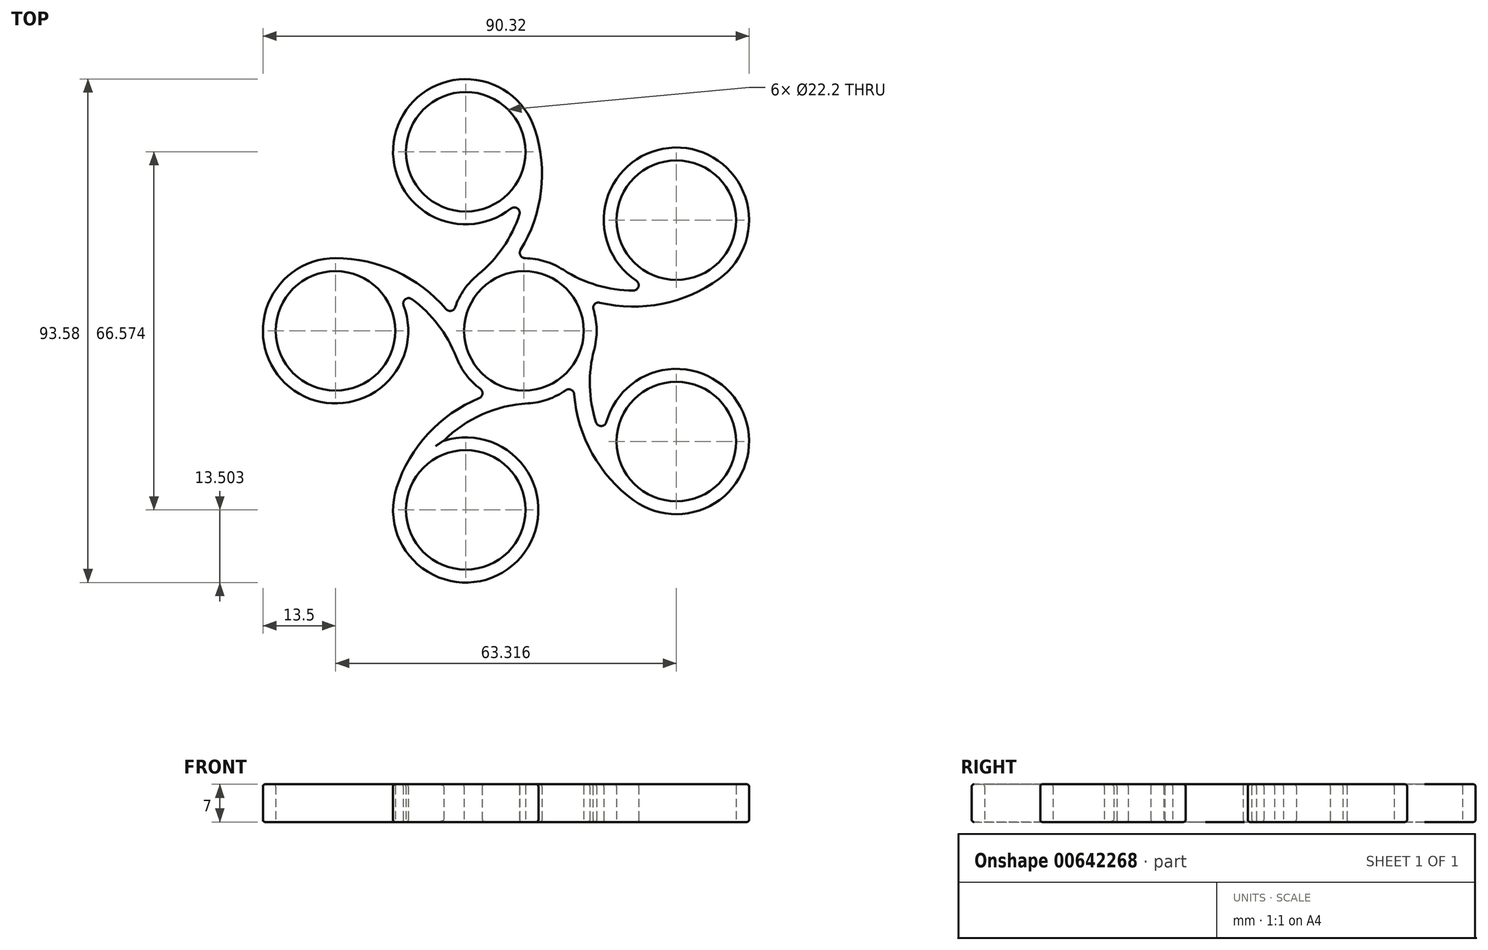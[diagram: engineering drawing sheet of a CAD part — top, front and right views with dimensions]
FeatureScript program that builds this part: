
annotation { "Feature Type Name" : "Feature", "Feature Type Description" : "" }
export const myFeature = defineFeature(function(context is Context, id is Id, definition is map)
    precondition{}
    {
        {
            var Q0;
            Q0=qCreatedBy(makeId("Top.planeOp"),FACE);
            var sketch = newSketch(context, id + "F0", { "sketchPlane" : qUnion([Q0])});
            skCircle(sketch, "E0", {"center": v(0, 0) * mm, "radius": 11.1 * mm});
            skCircle(sketch, "E1", {"center": v(0, 0) * mm, "radius": 13.5 * mm});
            skLineSegment(sketch, "E2", {"start": v(0, 0) * mm, "end": v(-35, 0) * mm, "construction": true});
            skCircle(sketch, "E3", {"center": v(-35, 0) * mm, "radius": 11.1 * mm});
            skCircle(sketch, "E4", {"center": v(-35, 0) * mm, "radius": 13.5 * mm});
            skLineSegment(sketch, "E5", {"start": v(-35, 0) * mm, "end": v(-35, -13.5) * mm, "construction": true});
            skLineSegment(sketch, "E6", {"start": v(0, 0) * mm, "end": v(0, 13.5) * mm, "construction": true});
            skLineSegment(sketch, "E7", {"start": v(-35, 0) * mm, "end": v(-25.45, -9.55) * mm, "construction": true});
            skLineSegment(sketch, "E8", {"start": v(0, 0) * mm, "end": v(-9.55, 9.55) * mm});
            skLineSegment(sketch, "E9", {"start": v(0, 0) * mm, "end": v(0, -13.5) * mm, "construction": true});
            skLineSegment(sketch, "E10", {"start": v(0, 0) * mm, "end": v(-9.55, -9.55) * mm, "construction": true});
            skArc(sketch, "E11.trimOffspring", {"start": v(-12.6, -4.86) * mm, "mid": v(-17.14, 2.55) * mm, "end": v(-24.02, 7.86) * mm});
            skArc(sketch, "E12.trimOffspring", {"start": v(-13.26, 2.52) * mm, "mid": v(-22.82, 10.6) * mm, "end": v(-35, 13.5) * mm});
            skArc(sketch, "E13.1.0", {"start": v(0.73, -13.48) * mm, "mid": v(-7.72, -15.51) * mm, "end": v(-14.9, -20.42) * mm});
            skCircle(sketch, "E13.1.1", {"center": v(-10.82, -33.29) * mm, "radius": 13.5 * mm});
            skArc(sketch, "E13.1.2", {"start": v(-6.5, -11.84) * mm, "mid": v(-17.13, -18.43) * mm, "end": v(-23.65, -29.12) * mm});
            skLineSegment(sketch, "E13.1.3", {"start": v(-10.82, -33.29) * mm, "end": v(2.02, -37.46) * mm, "construction": true});
            skCircle(sketch, "E13.1.4", {"center": v(-10.82, -33.29) * mm, "radius": 11.1 * mm});
            skLineSegment(sketch, "E13.1.5", {"start": v(-10.82, -33.29) * mm, "end": v(1.21, -27.16) * mm, "construction": true});
            skArc(sketch, "E13.2.0", {"start": v(13.05, -3.47) * mm, "mid": v(12.37, -12.14) * mm, "end": v(14.82, -20.48) * mm});
            skCircle(sketch, "E13.2.1", {"center": v(28.32, -20.57) * mm, "radius": 13.5 * mm});
            skArc(sketch, "E13.2.2", {"start": v(9.25, -9.83) * mm, "mid": v(12.23, -21.99) * mm, "end": v(20.38, -31.5) * mm});
            skLineSegment(sketch, "E13.2.3", {"start": v(28.32, -20.57) * mm, "end": v(36.25, -9.65) * mm, "construction": true});
            skCircle(sketch, "E13.2.4", {"center": v(28.32, -20.57) * mm, "radius": 11.1 * mm});
            skLineSegment(sketch, "E13.2.5", {"start": v(28.32, -20.57) * mm, "end": v(26.2, -7.24) * mm, "construction": true});
            skArc(sketch, "E13.3.0", {"start": v(7.33, 11.33) * mm, "mid": v(15.36, 8.01) * mm, "end": v(24.05, 7.76) * mm});
            skCircle(sketch, "E13.3.1", {"center": v(28.32, 20.57) * mm, "radius": 13.5 * mm});
            skArc(sketch, "E13.3.2", {"start": v(12.2, 5.76) * mm, "mid": v(24.7, 4.84) * mm, "end": v(36.25, 9.65) * mm});
            skLineSegment(sketch, "E13.3.3", {"start": v(28.32, 20.57) * mm, "end": v(20.38, 31.5) * mm, "construction": true});
            skCircle(sketch, "E13.3.4", {"center": v(28.32, 20.57) * mm, "radius": 11.1 * mm});
            skLineSegment(sketch, "E13.3.5", {"start": v(28.32, 20.57) * mm, "end": v(14.98, 22.68) * mm, "construction": true});
            skArc(sketch, "E13.4.0", {"start": v(-8.51, 10.48) * mm, "mid": v(-2.87, 17.09) * mm, "end": v(0.05, 25.27) * mm});
            skCircle(sketch, "E13.4.1", {"center": v(-10.82, 33.29) * mm, "radius": 13.5 * mm});
            skArc(sketch, "E13.4.2", {"start": v(-1.7, 13.4) * mm, "mid": v(3.03, 24.98) * mm, "end": v(2.02, 37.46) * mm});
            skLineSegment(sketch, "E13.4.3", {"start": v(-10.82, 33.29) * mm, "end": v(-23.65, 29.12) * mm, "construction": true});
            skCircle(sketch, "E13.4.4", {"center": v(-10.82, 33.29) * mm, "radius": 11.1 * mm});
            skLineSegment(sketch, "E13.4.5", {"start": v(-10.82, 33.29) * mm, "end": v(-16.94, 21.26) * mm, "construction": true});
            skSolve(sketch);
        }
        {
            var Q0;
            Q0=makeQuery(id+"F0.imprint","IMPRINT",FACE,{"disambiguationData":[TD([[makeQuery(id+"F0.imprint","IMPRINT",EDGE,{"derivedFrom":sQuery(id+"F0.wireOp",EDGE,"E0")}),-1.0]])]});
            var Q1;
            {var subQ0=sQuery(id+"F0.wireOp",EDGE,"e56zxMKM-Kjhy-064L-GIG7-PTHqFccnnUyJ");var subQ1=sQuery(id+"F0.wireOp",EDGE,"E1");var subQ2=makeQuery(id+"F0.imprint","INTERSECT",VERTEX,{"derivedFrom":[subQ1,subQ0]});Q1=makeQuery(id+"F0.imprint","IMPRINT",FACE,{"disambiguationData":[TD([[makeQuery(id+"F0.imprint","IMPRINT",EDGE,{"disambiguationData":[TD([[subQ2,-1.0]])],"derivedFrom":subQ1}),-1.0]])]});}
            var Q2;
            Q2=makeQuery(id+"F0.imprint","IMPRINT",FACE,{"disambiguationData":[TD([[makeQuery(id+"F0.imprint","IMPRINT",EDGE,{"derivedFrom":sQuery(id+"F0.wireOp",EDGE,"0e4e4f05-918f-47c3-9332-bcd5f5d39093.1.4.0")}),-1.0]])]});
            var Q3;
            {var subQ0=sQuery(id+"F0.wireOp",EDGE,"2f779958-1fc4-4bb9-a079-996d55da559e.1.0");var subQ1=sQuery(id+"F0.wireOp",EDGE,"E1");var subQ2=makeQuery(id+"F0.imprint","INTERSECT",VERTEX,{"derivedFrom":[subQ1,subQ0]});Q3=makeQuery(id+"F0.imprint","IMPRINT",FACE,{"disambiguationData":[TD([[makeQuery(id+"F0.imprint","IMPRINT",EDGE,{"disambiguationData":[TD([[subQ2,-1.0]])],"derivedFrom":subQ1}),-1.0]])]});}
            var Q4;
            Q4=makeQuery(id+"F0.imprint","IMPRINT",FACE,{"disambiguationData":[TD([[makeQuery(id+"F0.imprint","IMPRINT",EDGE,{"derivedFrom":sQuery(id+"F0.wireOp",EDGE,"E3")}),-1.0]])]});
            var Q5;
            {var subQ0=sQuery(id+"F0.wireOp",EDGE,"2f779958-1fc4-4bb9-a079-996d55da559e.2.0");var subQ1=sQuery(id+"F0.wireOp",EDGE,"E1");var subQ2=makeQuery(id+"F0.imprint","INTERSECT",VERTEX,{"derivedFrom":[subQ1,subQ0]});Q5=makeQuery(id+"F0.imprint","IMPRINT",FACE,{"disambiguationData":[TD([[makeQuery(id+"F0.imprint","IMPRINT",EDGE,{"disambiguationData":[TD([[subQ2,-1.0]])],"derivedFrom":subQ1}),-1.0]])]});}
            var Q6;
            Q6=makeQuery(id+"F0.imprint","IMPRINT",FACE,{"disambiguationData":[TD([[makeQuery(id+"F0.imprint","IMPRINT",EDGE,{"derivedFrom":sQuery(id+"F0.wireOp",EDGE,"2dce2605-6ec3-4248-8eab-4bc886ecd383.1.0")}),-1.0]])]});
            var Q7;
            {var subQ0=sQuery(id+"F0.wireOp",EDGE,"2f779958-1fc4-4bb9-a079-996d55da559e.3.0");var subQ1=sQuery(id+"F0.wireOp",EDGE,"E1");var subQ2=makeQuery(id+"F0.imprint","INTERSECT",VERTEX,{"derivedFrom":[subQ1,subQ0]});Q7=makeQuery(id+"F0.imprint","IMPRINT",FACE,{"disambiguationData":[TD([[makeQuery(id+"F0.imprint","IMPRINT",EDGE,{"disambiguationData":[TD([[subQ2,-1.0]])],"derivedFrom":subQ1}),-1.0]])]});}
            var Q8;
            Q8=makeQuery(id+"F0.imprint","IMPRINT",FACE,{"disambiguationData":[TD([[makeQuery(id+"F0.imprint","IMPRINT",EDGE,{"derivedFrom":sQuery(id+"F0.wireOp",EDGE,"2dce2605-6ec3-4248-8eab-4bc886ecd383.2.0")}),-1.0]])]});
            var Q9;
            {var subQ0=sQuery(id+"F0.wireOp",EDGE,"2f779958-1fc4-4bb9-a079-996d55da559e.4.0");var subQ1=sQuery(id+"F0.wireOp",EDGE,"E1");var subQ2=makeQuery(id+"F0.imprint","INTERSECT",VERTEX,{"derivedFrom":[subQ1,subQ0]});Q9=makeQuery(id+"F0.imprint","IMPRINT",FACE,{"disambiguationData":[TD([[makeQuery(id+"F0.imprint","IMPRINT",EDGE,{"disambiguationData":[TD([[subQ2,-1.0]])],"derivedFrom":subQ1}),-1.0]])]});}
            var Q10;
            Q10=makeQuery(id+"F0.imprint","IMPRINT",FACE,{"disambiguationData":[TD([[makeQuery(id+"F0.imprint","IMPRINT",EDGE,{"derivedFrom":sQuery(id+"F0.wireOp",EDGE,"0e4e4f05-918f-47c3-9332-bcd5f5d39093.1.3.0")}),-1.0]])]});
            var Q11;
            Q11=makeQuery(id+"F0.imprint","IMPRINT",FACE,{"disambiguationData":[TD([[makeQuery(id+"F0.imprint","IMPRINT",EDGE,{"derivedFrom":sQuery(id+"F0.wireOp",EDGE,"E13.4.4")}),-1.0]])]});
            var Q12;
            Q12=makeQuery(id+"F0.imprint","IMPRINT",FACE,{"disambiguationData":[TD([[makeQuery(id+"F0.imprint","IMPRINT",EDGE,{"derivedFrom":sQuery(id+"F0.wireOp",EDGE,"E13.3.4")}),-1.0]])]});
            var Q13;
            Q13=makeQuery(id+"F0.imprint","IMPRINT",FACE,{"disambiguationData":[TD([[makeQuery(id+"F0.imprint","IMPRINT",EDGE,{"derivedFrom":sQuery(id+"F0.wireOp",EDGE,"E13.2.4")}),-1.0]])]});
            var Q14;
            Q14=makeQuery(id+"F0.imprint","IMPRINT",FACE,{"disambiguationData":[TD([[makeQuery(id+"F0.imprint","IMPRINT",EDGE,{"derivedFrom":sQuery(id+"F0.wireOp",EDGE,"E13.1.4")}),-1.0]])]});
            extrude(context, id + "F1", {"entities" : qUnion([Q0, Q1, Q2, Q3, Q4, Q5, Q6, Q7, Q8, Q9, Q10, Q11, Q12, Q13, Q14]), "depth" : 7 * mm, "offsetDistance" : 25 * mm});
        }
        {
            var Q0;
            Q0=makeQuery(id+"F1.opExtrude","SWEPT_EDGE",EDGE,{"disambiguationData":[OSD([sQuery(id+"F0.wireOp",EDGE,"E4"),sQuery(id+"F0.wireOp",EDGE,"E11.trimOffspring")])]});
            var Q1;
            Q1=makeQuery(id+"F1.opExtrude","SWEPT_EDGE",EDGE,{"disambiguationData":[OSD([sQuery(id+"F0.wireOp",EDGE,"E13.4.0"),sQuery(id+"F0.wireOp",EDGE,"E13.4.1")])]});
            var Q2;
            Q2=makeQuery(id+"F1.opExtrude","SWEPT_EDGE",EDGE,{"disambiguationData":[OSD([sQuery(id+"F0.wireOp",EDGE,"E13.3.0"),sQuery(id+"F0.wireOp",EDGE,"E13.3.1")])]});
            var Q3;
            Q3=makeQuery(id+"F1.opExtrude","SWEPT_EDGE",EDGE,{"disambiguationData":[OSD([sQuery(id+"F0.wireOp",EDGE,"E1"),sQuery(id+"F0.wireOp",EDGE,"E13.1.2")])]});
            var Q4;
            Q4=makeQuery(id+"F1.opExtrude","SWEPT_EDGE",EDGE,{"disambiguationData":[OSD([sQuery(id+"F0.wireOp",EDGE,"E13.2.0"),sQuery(id+"F0.wireOp",EDGE,"E13.2.1")])]});
            var Q5;
            Q5=makeQuery(id+"F1.opExtrude","SWEPT_EDGE",EDGE,{"disambiguationData":[OSD([sQuery(id+"F0.wireOp",EDGE,"E1"),sQuery(id+"F0.wireOp",EDGE,"E13.4.2")])]});
            var Q6;
            Q6=makeQuery(id+"F1.opExtrude","SWEPT_EDGE",EDGE,{"disambiguationData":[OSD([sQuery(id+"F0.wireOp",EDGE,"E1"),sQuery(id+"F0.wireOp",EDGE,"E13.3.2")])]});
            var Q7;
            Q7=makeQuery(id+"F1.opExtrude","SWEPT_EDGE",EDGE,{"disambiguationData":[OSD([sQuery(id+"F0.wireOp",EDGE,"E1"),sQuery(id+"F0.wireOp",EDGE,"E13.2.2")])]});
            var Q8;
            Q8=makeQuery(id+"F1.opExtrude","SWEPT_EDGE",EDGE,{"disambiguationData":[OSD([sQuery(id+"F0.wireOp",EDGE,"E1"),sQuery(id+"F0.wireOp",EDGE,"E12.trimOffspring")])]});
            fillet(context, id + "F2", {"entities" : qUnion([Q0, Q1, Q2, Q3, Q4, Q5, Q6, Q7, Q8]), "radius" : 1 * mm, "tangentPropagation" : true, "allowEdgeOverflow" : false});
        }
        {
            var Q0;
            Q0=makeQuery(id+"F1.opExtrude","CAP_FACE",FACE,{"disambiguationData":[OSD([sQuery(id+"F0.wireOp",EDGE,"E0"),sQuery(id+"F0.wireOp",EDGE,"E1"),sQuery(id+"F0.wireOp",EDGE,"E3"),sQuery(id+"F0.wireOp",EDGE,"E4"),sQuery(id+"F0.wireOp",EDGE,"E11.trimOffspring"),sQuery(id+"F0.wireOp",EDGE,"E12.trimOffspring"),sQuery(id+"F0.wireOp",EDGE,"E13.1.0"),sQuery(id+"F0.wireOp",EDGE,"E13.1.1"),sQuery(id+"F0.wireOp",EDGE,"E13.1.2"),sQuery(id+"F0.wireOp",EDGE,"E13.1.4"),sQuery(id+"F0.wireOp",EDGE,"E13.2.0"),sQuery(id+"F0.wireOp",EDGE,"E13.2.1"),sQuery(id+"F0.wireOp",EDGE,"E13.2.2"),sQuery(id+"F0.wireOp",EDGE,"E13.2.4"),sQuery(id+"F0.wireOp",EDGE,"E13.3.0"),sQuery(id+"F0.wireOp",EDGE,"E13.3.1"),sQuery(id+"F0.wireOp",EDGE,"E13.3.2"),sQuery(id+"F0.wireOp",EDGE,"E13.3.4"),sQuery(id+"F0.wireOp",EDGE,"E13.4.0"),sQuery(id+"F0.wireOp",EDGE,"E13.4.1"),sQuery(id+"F0.wireOp",EDGE,"E13.4.2"),sQuery(id+"F0.wireOp",EDGE,"E13.4.4")])],"isStart":false});
            var Q1;
            Q1=makeQuery(id+"F1.opExtrude","CAP_EDGE",EDGE,{"disambiguationData":[OSD([sQuery(id+"F0.wireOp",EDGE,"E13.1.1")])],"isStart":true});
            fillet(context, id + "F3", {"entities" : qUnion([Q0, Q1]), "radius" : .4 * mm, "tangentPropagation" : true, "allowEdgeOverflow" : false});
        }
    });
